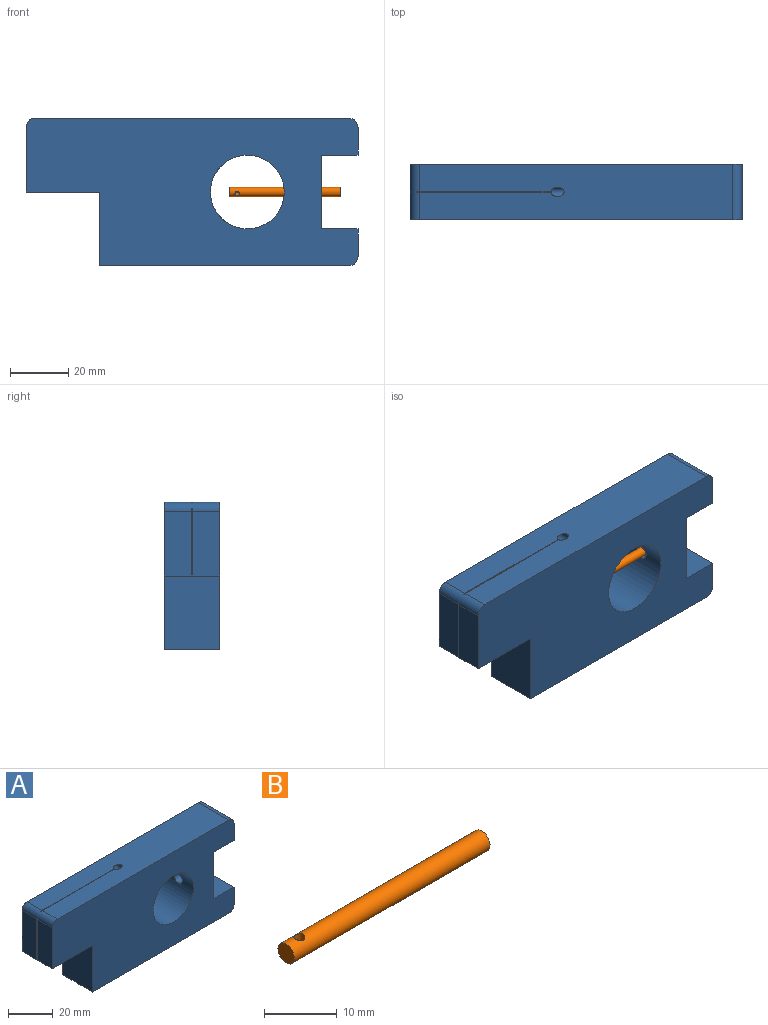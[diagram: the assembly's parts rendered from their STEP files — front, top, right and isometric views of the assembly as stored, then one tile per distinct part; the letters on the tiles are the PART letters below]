
ASSEMBLY  parts=2 mates=1
PART A: 23 faces, bbox 114.3x19.1x55.3 mm
  f0: plane 22.23x9.4mm, normal (-1,0,0), area 208.9mm2, adj f7,f15,f19,f20
  f1: plane 22.23x9.4mm, normal (-1,0,0), area 208.9mm2, adj f7,f14,f19,f20
  f2: cylinder r=1.59mm len=19.85mm, axis (0.71,0,-0.71), area 232.6mm2, adj f5,f6,f18
  f3: plane 85.73x19.05mm, normal (0,0,-1), area 1616mm2, adj f4,f8,f14,f15,f17,f22
  f4: cylinder r=1.59mm len=19.85mm, axis (0.71,0,0.71), area 232.6mm2, adj f3,f5,f17
  f5: cylinder r=12.7mm len=25.4mm, axis (0,1,0), area 1486.4mm2, adj f2,f4,f14,f15,f16
  f6: plane 107.95x19.05mm, normal (0,0,1), area 2033.7mm2, adj f2,f14,f15,f18,f19,f21
  f7: plane 25.4x19.05mm, normal (0,0,-1), area 483.8mm2, adj f0,f1,f8,f14,f15,f20
  f8: plane 25.4x19.05mm, normal (-1,0,0), area 483.8mm2, adj f3,f7,f14,f15,f17
  f9: plane 19.05x9.53mm, normal (1,0,0), area 181.5mm2, adj f10,f14,f15,f22
  f10: plane 19.05x12.7mm, normal (0,0,1), area 241.9mm2, adj f9,f11,f14,f15
  f11: plane 25.4x19.05mm, normal (1,0,0), area 466.1mm2, adj f10,f12,f14,f15,f16
  f12: plane 19.05x12.7mm, normal (0,0,-1), area 241.9mm2, adj f11,f13,f14,f15
  f13: plane 19.05x9.53mm, normal (1,0,0), area 181.5mm2, adj f12,f14,f15,f21
  f14: plane 114.3x50.8mm, normal (0,-1,0), area 4325.5mm2, adj f1,f3,f5,f6,f7,f8,f9,f10
  f15: plane 114.3x50.8mm, normal (0,1,0), area 4325.5mm2, adj f0,f3,f5,f6,f7,f8,f9,f10
  f16: cylinder r=2.38mm len=12.93mm, axis (1,0,0), area 193.4mm2, adj f5,f11
  f17: cylinder r=0.13mm len=23.16mm, axis (-1,0,0), area 9.2mm2, adj f3,f4,f8
  f18: cylinder r=0.13mm len=46.4mm, axis (-1,0,0), area 18.4mm2, adj f2,f6,f19
  f19: cylinder r=3.17mm len=19.05mm, axis (0,-1,0), area 94.6mm2, adj f0,f1,f6,f14,f15,f18,f20
  f20: cylinder r=0.13mm len=23.12mm, axis (0,0,1), area 9.1mm2, adj f0,f1,f7,f19
  f21: cylinder r=3.17mm len=19.05mm, axis (0,1,0), area 95mm2, adj f6,f13,f14,f15
  f22: cylinder r=3.17mm len=19.05mm, axis (0,-1,0), area 95mm2, adj f3,f9,f14,f15
PART B: 4 faces, bbox 38.1x3.2x3.2 mm
  f0: cylinder r=1.59mm len=38.1mm, axis (1,0,0), area 375.9mm2, adj f1,f2,f3
  f1: plane 3.18x3.18mm, normal (-1,0,0), area 7.9mm2, adj f0
  f2: plane 3.18x3.18mm, normal (1,0,0), area 7.9mm2, adj f0
  f3: cylinder r=0.79mm len=3.18mm, axis (0,0,1), area 14.8mm2, adj f0
PLACE A t=(7.94,0,25.4)mm
PLACE B rot(axis=(1,0,0),112.8deg) t=(40.03,-9.53,25.4)mm
MATE cylindrical A.f16 <-> B.f0  axis (1,0,0) through (33.34,-9.52,25.4)mm
